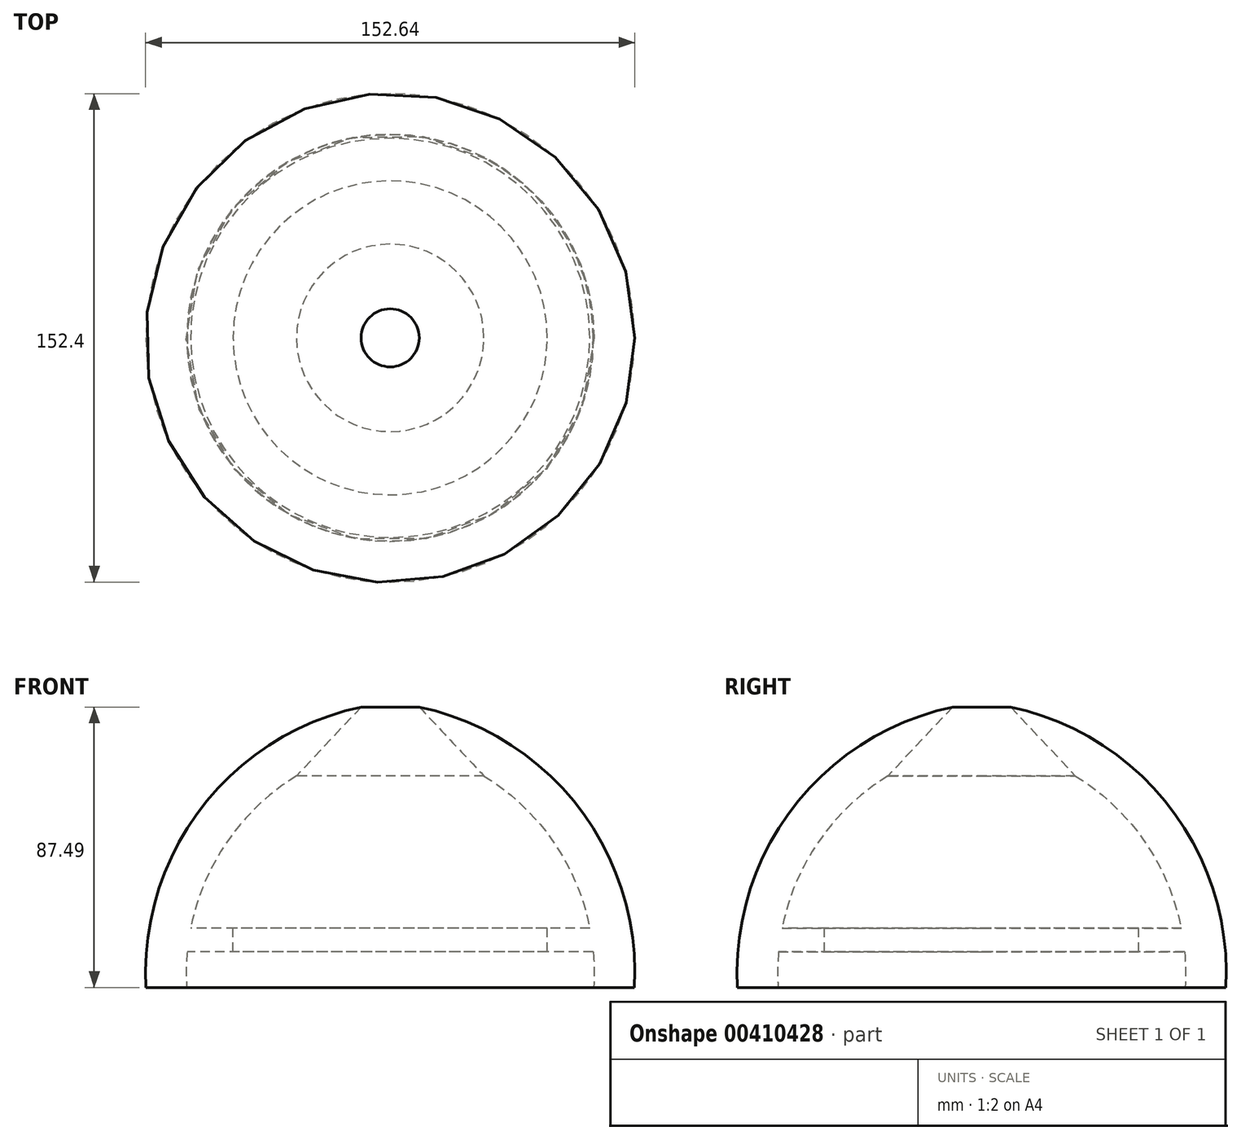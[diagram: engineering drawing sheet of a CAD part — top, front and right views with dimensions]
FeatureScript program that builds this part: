
annotation { "Feature Type Name" : "Feature", "Feature Type Description" : "" }
export const myFeature = defineFeature(function(context is Context, id is Id, definition is map)
    precondition{}
    {
        {
            var Q0;
            Q0=qCreatedBy(makeId("Front.planeOp"),FACE);
            var sketch = newSketch(context, id + "F0", { "sketchPlane" : qUnion([Q0])});
            skLineSegment(sketch, "E0", {"start": v(63.5, 0) * mm, "end": v(76.2, 0) * mm});
            skArc(sketch, "E1", {"start": v(76.2, 0) * mm, "mid": v(58.8, 56.16) * mm, "end": v(9.06, 87.5) * mm});
            skArc(sketch, "E2", {"start": v(63.5, 0) * mm, "mid": v(63.63, 5.54) * mm, "end": v(63.34, 11.08) * mm});
            skLineSegment(sketch, "E3", {"start": v(62.27, 18.47) * mm, "end": v(49, 18.47) * mm});
            skLineSegment(sketch, "E4", {"start": v(49, 18.47) * mm, "end": v(49, 11.08) * mm});
            skLineSegment(sketch, "E5", {"start": v(49, 11.08) * mm, "end": v(63.34, 11.08) * mm});
            skArc(sketch, "E6.trimOffspring", {"start": v(62.27, 18.47) * mm, "mid": v(50.73, 45.7) * mm, "end": v(29.25, 66.01) * mm});
            skLineSegment(sketch, "E7", {"start": v(9.06, 87.5) * mm, "end": v(29.25, 66.01) * mm});
            skPoint(sketch, "E8.orphan", {"position": v(0, 88.9) * mm});
            skPoint(sketch, "E9.orphan", {"position": v(0, 76.2) * mm});
            skLineSegment(sketch, "E10", {"start": v(0, 88.9) * mm, "end": v(0, 76.2) * mm});
            skSolve(sketch);
        }
        {
            var Q0;
            Q0=makeQuery(id+"F0.imprint","IMPRINT",FACE,{"disambiguationData":[TD([[makeQuery(id+"F0.imprint","IMPRINT",EDGE,{"derivedFrom":sQuery(id+"F0.wireOp",EDGE,"E0")}),1.0]])]});
            var Q1;
            Q1=sQuery(id+"F0.wireOp",EDGE,"E10");
            revolve(context, id + "F1", {"entities" : qUnion([Q0]), "axis" : qUnion([Q1]), "revolveType" : RevolveType.FULL});
        }
    });
